# Revit family: sh-2201
name_source: partatom
category: Lighting Fixtures
revit_build: Autodesk Revit 2017 (Build: 20160225_1515(x64)
units: mm (PartAtom-declared; Revit-internal decimal feet)

## family parameters
Always vertical = Yes
Cut with Voids When Loaded = No
Host = Ceiling
Light Source = No
OmniClass Number = 23.80.70.11
OmniClass Title = Luminaries for Internal Lighting
Part Type = Normal
Room Calculation Point = No
Round Connector Dimension = Use Diameter
Shared = No

## types (2) — shared parameters
Body Material = Plaster
Body color = white body
Cutting Diameter = 12.0 cm
Default Elevation = 0.0 cm
Diameter = 12.0 cm
Flicker = Free Flicker
Height = 10.7 cm
Lamp = GU10&GU5.3
Manufacturer = SHOA
Model = SH-2201
Protection Class = class I
Type medule = SMD
URL = https://www.shoaco.com
Voltage/Frequency = 230V-50HZ
Website = www.shoaco.com
color rendering index(CRI) = 80
consumption current = 0 A
instalation = Recessed
wattage. = 7 W

## per-type parameters (varying)
| type | 3000k | 4000k | color temperature |
| SH-2201(Plaster-4000K-GU10&GU5.3) | No | Yes | 4000k |
| SH-2201(Plaster-3000K-GU10&GU5.3) | Yes | No | 3000k |

## geometry (parser evidence)
native form markers: Sweep x4
no freeform markers — native parametric forms only
